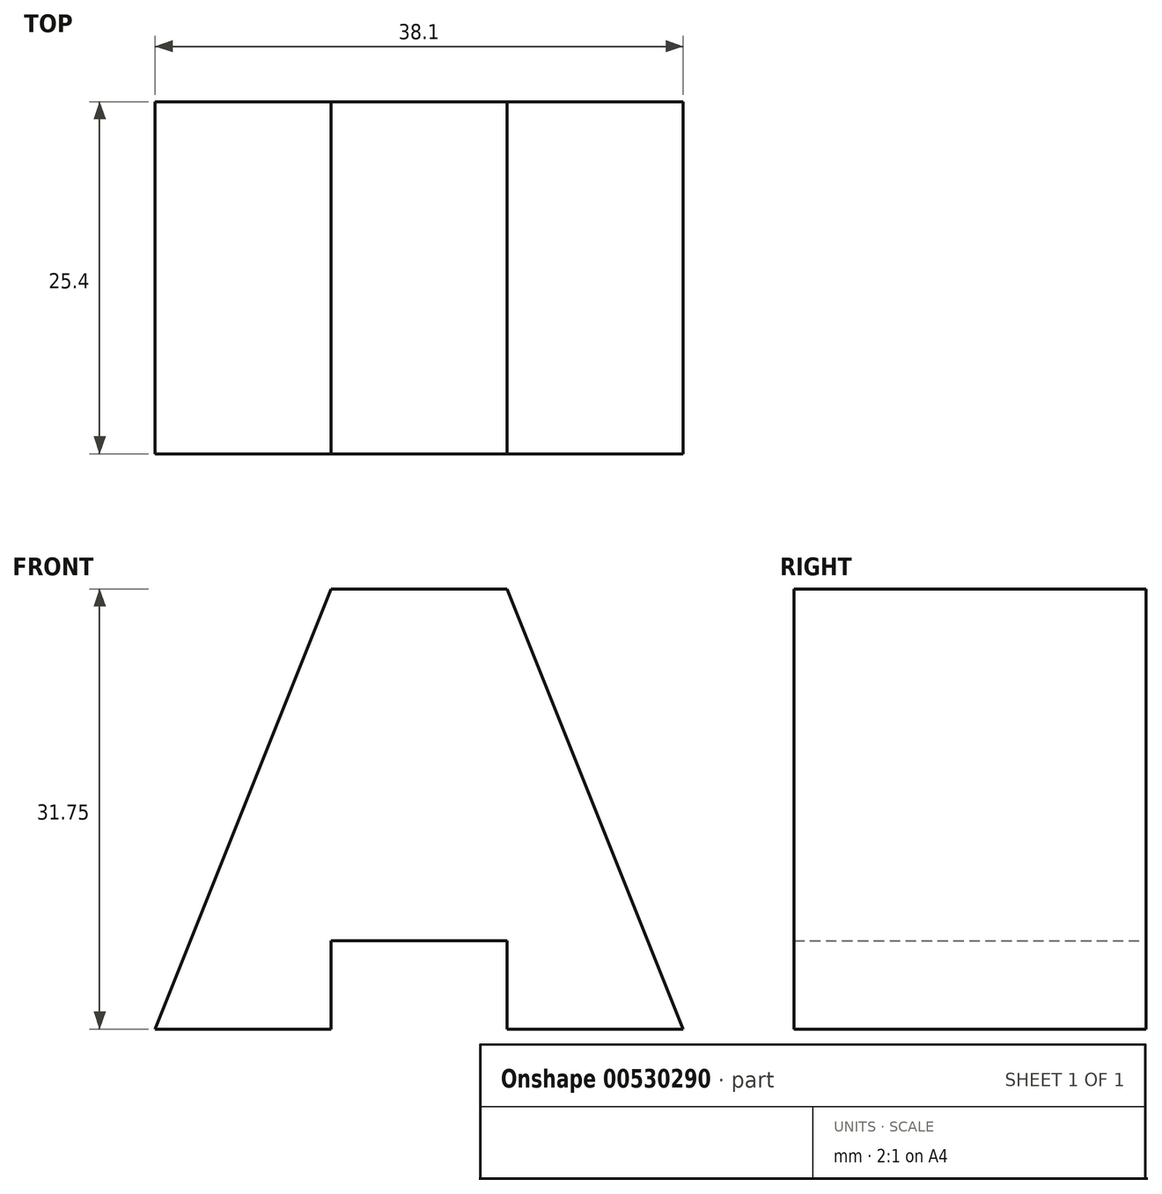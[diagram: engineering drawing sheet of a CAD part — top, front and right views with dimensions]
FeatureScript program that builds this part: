
annotation { "Feature Type Name" : "Feature", "Feature Type Description" : "" }
export const myFeature = defineFeature(function(context is Context, id is Id, definition is map)
    precondition{}
    {
        {
            var Q0;
            Q0=qCreatedBy(makeId("Front.planeOp"),FACE);
            var sketch = newSketch(context, id + "F0", { "sketchPlane" : qUnion([Q0])});
            skLineSegment(sketch, "E0", {"start": v(-25.4, 31.75) * mm, "end": v(12.7, 31.75) * mm});
            skLineSegment(sketch, "E1", {"start": v(12.7, 31.75) * mm, "end": v(12.7, 0) * mm});
            skLineSegment(sketch, "E2", {"start": v(-25.4, 31.75) * mm, "end": v(-25.4, 0) * mm});
            skLineSegment(sketch, "E3", {"start": v(-25.4, 0) * mm, "end": v(-12.7, 0) * mm});
            skLineSegment(sketch, "E4", {"start": v(-12.7, 0) * mm, "end": v(-12.7, 6.38) * mm});
            skLineSegment(sketch, "E5", {"start": v(-12.7, 6.38) * mm, "end": v(0, 6.38) * mm});
            skLineSegment(sketch, "E6", {"start": v(0, 6.38) * mm, "end": v(0, 0) * mm});
            skLineSegment(sketch, "E7", {"start": v(0, 0) * mm, "end": v(12.7, 0) * mm});
            skSolve(sketch);
        }
        {
            var Q0;
            Q0=makeQuery(id+"F0.imprint","IMPRINT",FACE,{"disambiguationData":[TD([[makeQuery(id+"F0.imprint","IMPRINT",EDGE,{"derivedFrom":sQuery(id+"F0.wireOp",EDGE,"E0")}),-1.0]])]});
            extrude(context, id + "F1", {"entities" : qUnion([Q0]), "depth" : 25.4 * mm, "offsetDistance" : 25.4 * mm});
        }
        {
            var Q0;
            Q0=makeQuery(id+"F1.opExtrude","CAP_FACE",FACE,{"disambiguationData":[OSD([sQuery(id+"F0.wireOp",EDGE,"E0"),sQuery(id+"F0.wireOp",EDGE,"E1"),sQuery(id+"F0.wireOp",EDGE,"E2"),sQuery(id+"F0.wireOp",EDGE,"E3"),sQuery(id+"F0.wireOp",EDGE,"E4"),sQuery(id+"F0.wireOp",EDGE,"E5"),sQuery(id+"F0.wireOp",EDGE,"E6"),sQuery(id+"F0.wireOp",EDGE,"E7")])],"isStart":false});
            var sketch = newSketch(context, id + "F2", { "sketchPlane" : qUnion([Q0])});
            skLineSegment(sketch, "E8", {"start": v(0, 31.75) * mm, "end": v(12.7, 0) * mm});
            skLineSegment(sketch, "E9", {"start": v(-12.7, 31.75) * mm, "end": v(-25.4, 0) * mm});
            skSolve(sketch);
        }
        {
            var Q0;
            {var subQ0=sQuery(id+"F2.wireOp",EDGE,"E9");Q0=makeQuery(id+"F2.imprint","IMPRINT",FACE,{"disambiguationData":[TD([[makeQuery(id+"F2.imprint","IMPRINT",EDGE,{"derivedFrom":subQ0}),-1.0]])]});}
            var Q1;
            {var subQ0=sQuery(id+"F2.wireOp",EDGE,"E8");Q1=makeQuery(id+"F2.imprint","IMPRINT",FACE,{"disambiguationData":[TD([[makeQuery(id+"F2.imprint","IMPRINT",EDGE,{"derivedFrom":subQ0}),1.0]])]});}
            extrude(context, id + "F3", {"entities" : qUnion([Q0, Q1]), "operationType" : NewBodyOperationType.REMOVE, "oppositeDirection" : true, "depth" : 25.4 * mm, "offsetDistance" : 25.4 * mm});
        }
    });
